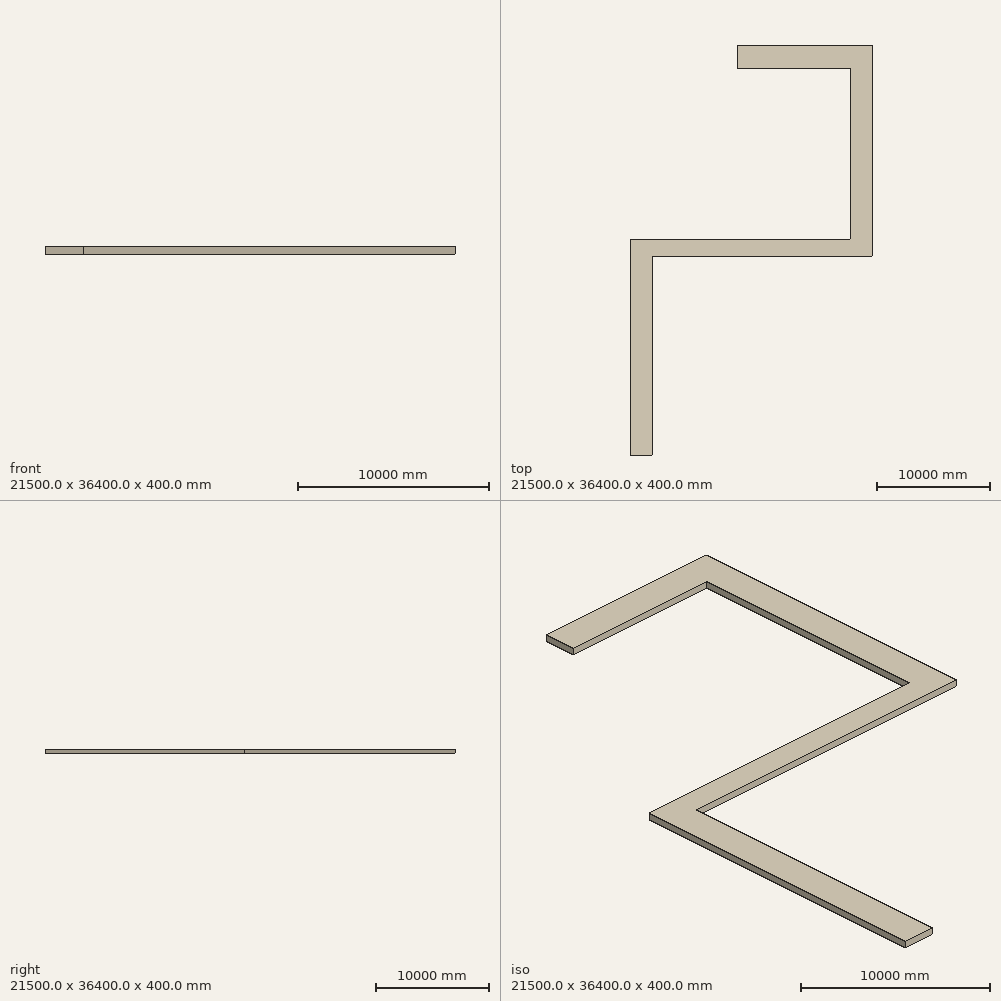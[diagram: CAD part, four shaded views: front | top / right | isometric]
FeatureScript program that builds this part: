
annotation { "Feature Type Name" : "Feature", "Feature Type Description" : "" }
export const myFeature = defineFeature(function(context is Context, id is Id, definition is map)
    precondition{}
    {
        {
            var Q0;
            Q0=qCreatedBy(makeId("Top.planeOp"),FACE);
            var sketch = newSketch(context, id + "F0", { "sketchPlane" : qUnion([Q0])});
            skLineSegment(sketch, "E0", {"start": v(0, 0) * mm, "end": v(0, -19200) * mm});
            skLineSegment(sketch, "E1", {"start": v(0, -19200) * mm, "end": v(2000, -19200) * mm});
            skLineSegment(sketch, "E2", {"start": v(2000, -19200) * mm, "end": v(2000, -1500) * mm});
            skLineSegment(sketch, "E3", {"start": v(2000, -1500) * mm, "end": v(21500, -1500) * mm});
            skLineSegment(sketch, "E4", {"start": v(21500, -1500) * mm, "end": v(21500, 0) * mm});
            skLineSegment(sketch, "E5", {"start": v(21500, 0) * mm, "end": v(0, 0) * mm});
            skSolve(sketch);
        }
        {
            var Q0;
            Q0 = qSketchRegion(id + "F0", true);
            extrude(context, id + "F1", {"entities" : qUnion([Q0]), "depth" : 400 * mm, "offsetDistance" : 25 * mm});
        }
        {
            var Q0;
            Q0=makeQuery(id+"F1.opExtrude","SWEPT_FACE",FACE,{"disambiguationData":[OSD([sQuery(id+"F0.wireOp",EDGE,"E5")])]});
            var sketch = newSketch(context, id + "F2", { "sketchPlane" : qUnion([Q0])});
            skLineSegment(sketch, "E6.bottom", {"start": v(-21500, 400) * mm, "end": v(-19500, 400) * mm});
            skLineSegment(sketch, "E6.top", {"start": v(-21500, 0) * mm, "end": v(-19500, 0) * mm});
            skLineSegment(sketch, "E6.left", {"start": v(-21500, 400) * mm, "end": v(-21500, 0) * mm});
            skLineSegment(sketch, "E6.right", {"start": v(-19500, 400) * mm, "end": v(-19500, 0) * mm});
            skSolve(sketch);
        }
        {
            var Q0;
            Q0 = qSketchRegion(id + "F2", true);
            extrude(context, id + "F3", {"entities" : qUnion([Q0]), "operationType" : NewBodyOperationType.ADD, "depth" : 17200 * mm, "offsetDistance" : 25 * mm});
        }
        {
            var Q0;
            Q0=makeQuery(id+"F3.opExtrude","SWEPT_FACE",FACE,{"disambiguationData":[OSD([sQuery(id+"F2.wireOp",EDGE,"E6.right")])]});
            var sketch = newSketch(context, id + "F4", { "sketchPlane" : qUnion([Q0])});
            skLineSegment(sketch, "E7.bottom", {"start": v(-17200, 400) * mm, "end": v(-15200, 400) * mm});
            skLineSegment(sketch, "E7.top", {"start": v(-17200, 0) * mm, "end": v(-15200, 0) * mm});
            skLineSegment(sketch, "E7.left", {"start": v(-17200, 400) * mm, "end": v(-17200, 0) * mm});
            skLineSegment(sketch, "E7.right", {"start": v(-15200, 400) * mm, "end": v(-15200, 0) * mm});
            skSolve(sketch);
        }
        {
            var Q0;
            Q0 = qSketchRegion(id + "F4", true);
            extrude(context, id + "F5", {"entities" : qUnion([Q0]), "operationType" : NewBodyOperationType.ADD, "depth" : 10000 * mm, "offsetDistance" : 25 * mm});
        }
    });
